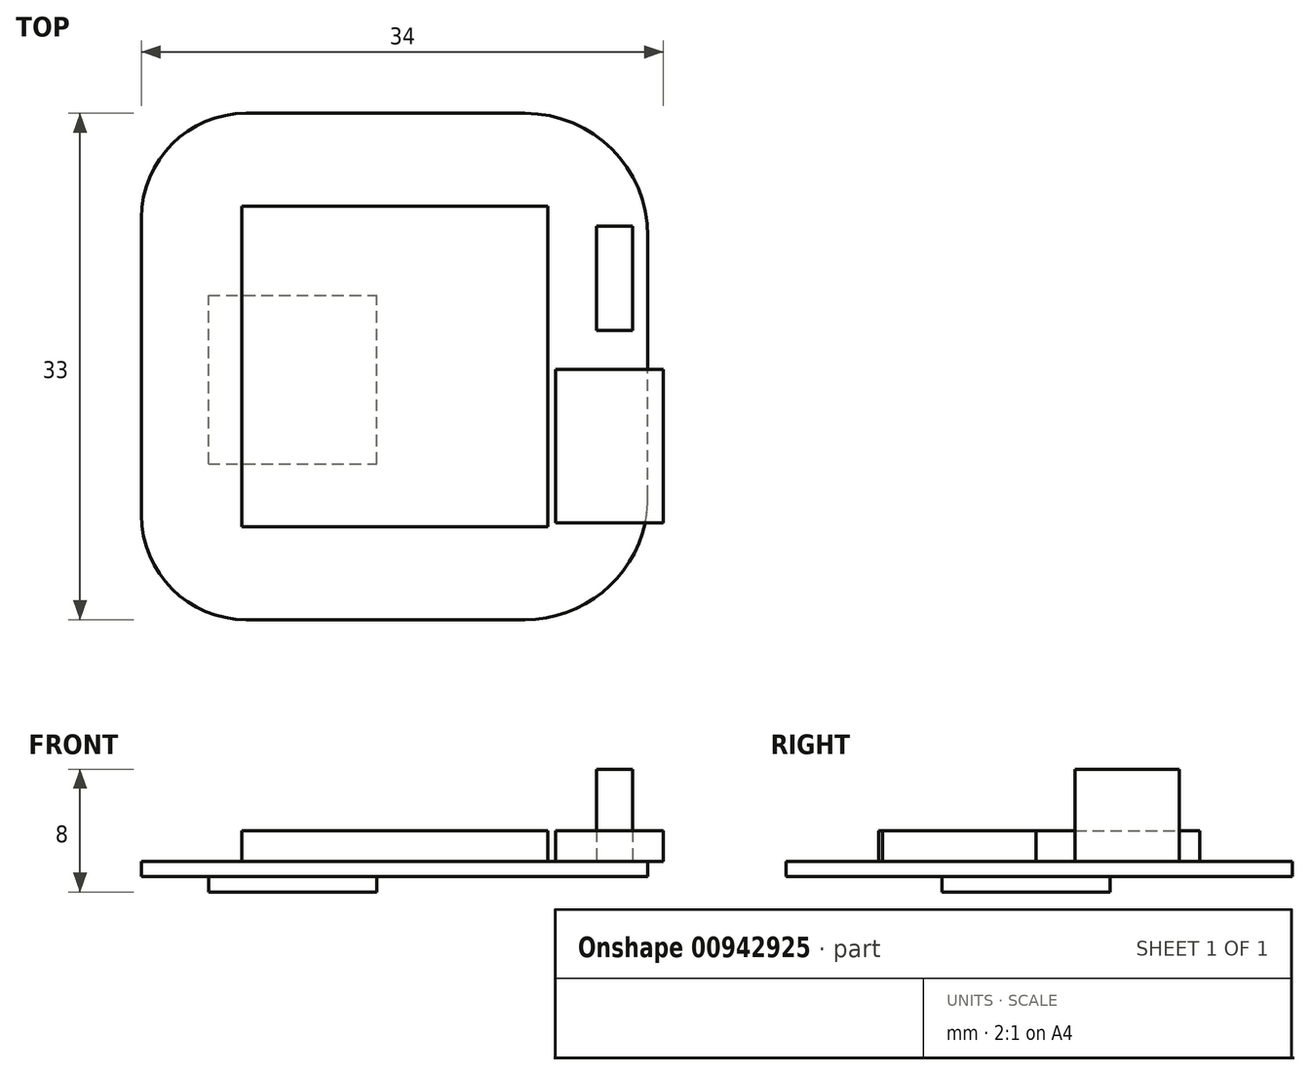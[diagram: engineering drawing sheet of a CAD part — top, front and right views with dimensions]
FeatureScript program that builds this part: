
annotation { "Feature Type Name" : "Feature", "Feature Type Description" : "" }
export const myFeature = defineFeature(function(context is Context, id is Id, definition is map)
    precondition{}
    {
        {
            var Q0;
            Q0=qCreatedBy(makeId("Top.planeOp"),FACE);
            var sketch = newSketch(context, id + "F0", { "sketchPlane" : qUnion([Q0])});
            skLineSegment(sketch, "E0.bottom", {"start": v(8.5, -16.5) * mm, "end": v(-9.67, -16.5) * mm});
            skLineSegment(sketch, "E0.top", {"start": v(8.5, 16.5) * mm, "end": v(-9.67, 16.5) * mm});
            skLineSegment(sketch, "E0.left", {"start": v(16.5, -8.5) * mm, "end": v(16.5, 8.5) * mm});
            skLineSegment(sketch, "E0.right", {"start": v(-16.5, -9.67) * mm, "end": v(-16.5, 9.67) * mm});
            skPoint(sketch, "E0.middle", {"position": v(0, 0) * mm});
            skPoint(sketch, "E1.visualSharp", {"position": v(-16.5, 16.5) * mm});
            skArc(sketch, "E1.filletArc", {"start": v(-9.67, 16.5) * mm, "mid": v(-14.5, 14.5) * mm, "end": v(-16.5, 9.67) * mm});
            skPoint(sketch, "E2.visualSharp", {"position": v(-16.5, -16.5) * mm});
            skArc(sketch, "E2.filletArc", {"start": v(-16.5, -9.67) * mm, "mid": v(-14.5, -14.5) * mm, "end": v(-9.67, -16.5) * mm});
            skPoint(sketch, "E3.visualSharp", {"position": v(16.5, 16.5) * mm});
            skArc(sketch, "E3.filletArc", {"start": v(16.5, 8.5) * mm, "mid": v(14.16, 14.16) * mm, "end": v(8.5, 16.5) * mm});
            skPoint(sketch, "E4.visualSharp", {"position": v(16.5, -16.5) * mm});
            skArc(sketch, "E4.filletArc", {"start": v(8.5, -16.5) * mm, "mid": v(14.16, -14.16) * mm, "end": v(16.5, -8.5) * mm});
            skSolve(sketch);
        }
        {
            var Q0;
            {var subQ5=sQuery(id+"F0.wireOp",EDGE,"E0.bottom");Q0=makeQuery(id+"F0.imprint","IMPRINT",FACE,{"disambiguationData":[TD([[makeQuery(id+"F0.imprint","IMPRINT",EDGE,{"derivedFrom":subQ5}),-1.0]])]});}
            extrude(context, id + "F1", {"entities" : qUnion([Q0]), "depth" : 1 * mm, "offsetDistance" : 25 * mm});
        }
        {
            var Q0;
            Q0=makeQuery(id+"F1.opExtrude","CAP_FACE",FACE,{"disambiguationData":[OSD([sQuery(id+"F0.wireOp",EDGE,"E0.bottom"),sQuery(id+"F0.wireOp",EDGE,"E0.top"),sQuery(id+"F0.wireOp",EDGE,"E0.left"),sQuery(id+"F0.wireOp",EDGE,"E0.right"),sQuery(id+"F0.wireOp",EDGE,"E1.filletArc"),sQuery(id+"F0.wireOp",EDGE,"E2.filletArc"),sQuery(id+"F0.wireOp",EDGE,"E3.filletArc"),sQuery(id+"F0.wireOp",EDGE,"E4.filletArc")])],"isStart":false});
            var sketch = newSketch(context, id + "F2", { "sketchPlane" : qUnion([Q0])});
            skLineSegment(sketch, "E5.bottom", {"start": v(17.5, -10.2) * mm, "end": v(10.5, -10.2) * mm});
            skLineSegment(sketch, "E5.top", {"start": v(17.5, -0.2) * mm, "end": v(10.5, -0.2) * mm});
            skLineSegment(sketch, "E5.left", {"start": v(17.5, -10.2) * mm, "end": v(17.5, -0.2) * mm});
            skLineSegment(sketch, "E5.right", {"start": v(10.5, -10.2) * mm, "end": v(10.5, -0.2) * mm});
            skPoint(sketch, "E5.middle", {"position": v(14, -5.2) * mm});
            skLineSegment(sketch, "E6.bottom", {"start": v(15.5, 2.34) * mm, "end": v(13.17, 2.34) * mm});
            skLineSegment(sketch, "E6.top", {"start": v(15.5, 9.14) * mm, "end": v(13.17, 9.14) * mm});
            skLineSegment(sketch, "E6.left", {"start": v(15.5, 2.34) * mm, "end": v(15.5, 9.14) * mm});
            skLineSegment(sketch, "E6.right", {"start": v(13.17, 2.34) * mm, "end": v(13.17, 9.14) * mm});
            skPoint(sketch, "E6.middle", {"position": v(14.33, 5.74) * mm});
            skSolve(sketch);
        }
        {
            var Q0;
            {var subQ5=sQuery(id+"F2.wireOp",EDGE,"E5.left");Q0=makeQuery(id+"F2.imprint","IMPRINT",FACE,{"disambiguationData":[TD([[makeQuery(id+"F2.imprint","IMPRINT",EDGE,{"derivedFrom":subQ5}),1.0]])]});}
            var Q1;
            {var subQ0=sQuery(id+"F2.wireOp",EDGE,"E5.right");Q1=makeQuery(id+"F2.imprint","IMPRINT",FACE,{"disambiguationData":[TD([[makeQuery(id+"F2.imprint","IMPRINT",EDGE,{"derivedFrom":subQ0}),-1.0]])]});}
            extrude(context, id + "F3", {"entities" : qUnion([Q0, Q1]), "operationType" : NewBodyOperationType.ADD, "depth" : 2 * mm, "offsetDistance" : 25 * mm});
        }
        {
            var Q0;
            Q0=makeQuery(id+"F1.opExtrude","CAP_FACE",FACE,{"disambiguationData":[OSD([sQuery(id+"F0.wireOp",EDGE,"E0.bottom"),sQuery(id+"F0.wireOp",EDGE,"E0.top"),sQuery(id+"F0.wireOp",EDGE,"E0.left"),sQuery(id+"F0.wireOp",EDGE,"E0.right"),sQuery(id+"F0.wireOp",EDGE,"E1.filletArc"),sQuery(id+"F0.wireOp",EDGE,"E2.filletArc"),sQuery(id+"F0.wireOp",EDGE,"E3.filletArc"),sQuery(id+"F0.wireOp",EDGE,"E4.filletArc")])],"isStart":false});
            var sketch = newSketch(context, id + "F4", { "sketchPlane" : qUnion([Q0])});
            skLineSegment(sketch, "E7.bottom", {"start": v(-9.97, -10.46) * mm, "end": v(9.97, -10.46) * mm});
            skLineSegment(sketch, "E7.top", {"start": v(-9.97, 10.46) * mm, "end": v(9.97, 10.46) * mm});
            skLineSegment(sketch, "E7.left", {"start": v(-9.97, -10.46) * mm, "end": v(-9.97, 10.46) * mm});
            skLineSegment(sketch, "E7.right", {"start": v(9.97, -10.46) * mm, "end": v(9.97, 10.46) * mm});
            skPoint(sketch, "E7.middle", {"position": v(0, 0) * mm});
            skSolve(sketch);
        }
        {
            var Q0;
            Q0=makeQuery(id+"F4.imprint","IMPRINT",FACE,{"disambiguationData":[TD([[makeQuery(id+"F4.imprint","IMPRINT",EDGE,{"derivedFrom":sQuery(id+"F4.wireOp",EDGE,"E7.bottom")}),1.0]])]});
            extrude(context, id + "F5", {"entities" : qUnion([Q0]), "operationType" : NewBodyOperationType.ADD, "depth" : 2 * mm, "offsetDistance" : 25 * mm});
        }
        {
            var Q0;
            Q0=makeQuery(id+"F2.imprint","IMPRINT",FACE,{"disambiguationData":[TD([[makeQuery(id+"F2.imprint","IMPRINT",EDGE,{"derivedFrom":sQuery(id+"F2.wireOp",EDGE,"E6.bottom")}),-1.0]])]});
            extrude(context, id + "F6", {"entities" : qUnion([Q0]), "operationType" : NewBodyOperationType.ADD, "depth" : 6 * mm, "offsetDistance" : 25 * mm});
        }
        {
            var Q0;
            Q0=makeQuery(id+"F1.opExtrude","CAP_FACE",FACE,{"disambiguationData":[OSD([sQuery(id+"F0.wireOp",EDGE,"E0.bottom"),sQuery(id+"F0.wireOp",EDGE,"E0.top"),sQuery(id+"F0.wireOp",EDGE,"E0.left"),sQuery(id+"F0.wireOp",EDGE,"E0.right"),sQuery(id+"F0.wireOp",EDGE,"E1.filletArc"),sQuery(id+"F0.wireOp",EDGE,"E2.filletArc"),sQuery(id+"F0.wireOp",EDGE,"E3.filletArc"),sQuery(id+"F0.wireOp",EDGE,"E4.filletArc")])],"isStart":true});
            var sketch = newSketch(context, id + "F7", { "sketchPlane" : qUnion([Q0])});
            skPoint(sketch, "E8.middle", {"position": v(0, 0) * mm});
            skLineSegment(sketch, "E9.bottom", {"start": v(-12.13, 6.35) * mm, "end": v(-1.17, 6.35) * mm});
            skLineSegment(sketch, "E9.top", {"start": v(-12.13, -4.62) * mm, "end": v(-1.17, -4.62) * mm});
            skLineSegment(sketch, "E9.left", {"start": v(-12.13, 6.35) * mm, "end": v(-12.13, -4.62) * mm});
            skLineSegment(sketch, "E9.right", {"start": v(-1.17, 6.35) * mm, "end": v(-1.17, -4.62) * mm});
            skSolve(sketch);
        }
        {
            var Q0;
            Q0=makeQuery(id+"F7.imprint","IMPRINT",FACE,{"disambiguationData":[TD([[makeQuery(id+"F7.imprint","IMPRINT",EDGE,{"derivedFrom":sQuery(id+"F7.wireOp",EDGE,"E9.bottom")}),-1.0]])]});
            extrude(context, id + "F8", {"entities" : qUnion([Q0]), "operationType" : NewBodyOperationType.ADD, "depth" : 1 * mm, "offsetDistance" : 25 * mm});
        }
    });
